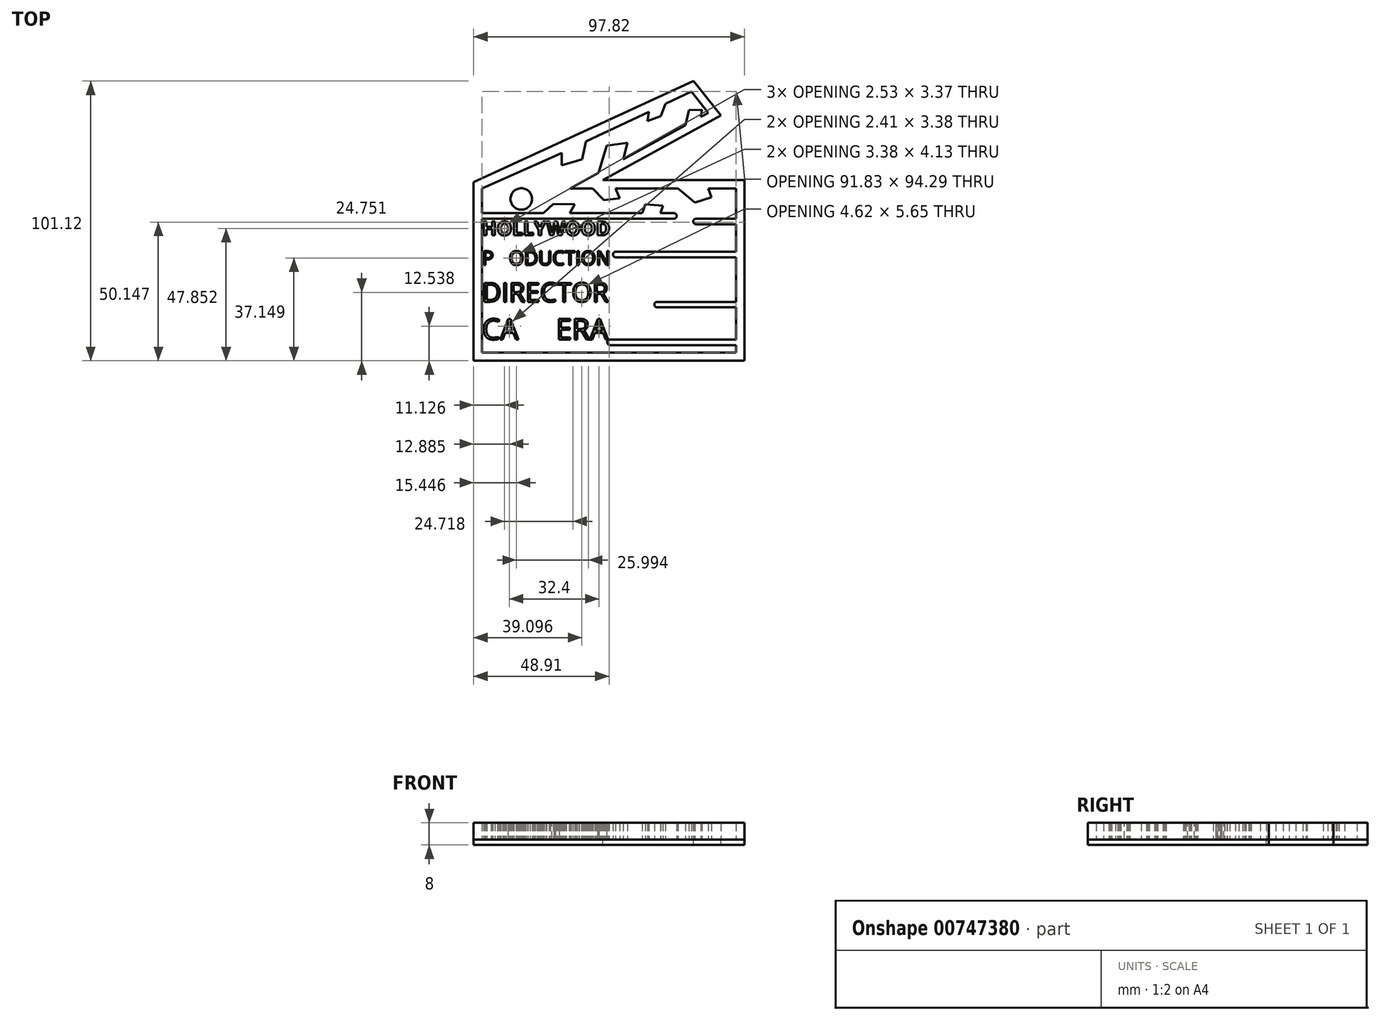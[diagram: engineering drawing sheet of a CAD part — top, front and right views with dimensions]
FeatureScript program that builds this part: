
annotation { "Feature Type Name" : "Feature", "Feature Type Description" : "" }
export const myFeature = defineFeature(function(context is Context, id is Id, definition is map)
    precondition{}
    {
        {
            var Q0;
            Q0=qCreatedBy(makeId("Top.planeOp"),FACE);
            var sketch = newSketch(context, id + "F0", { "sketchPlane" : qUnion([Q0])});
            skLineSegment(sketch, "E0", {"start": v(-11.38, 5.66) * mm, "end": v(-6.26, 5.66) * mm});
            skLineSegment(sketch, "E1", {"start": v(45.56, 5.66) * mm, "end": v(45.56, -5.33) * mm});
            skLineSegment(sketch, "E2", {"start": v(45.56, -53.68) * mm, "end": v(-46.26, -53.68) * mm});
            skLineSegment(sketch, "E3", {"start": v(-46.26, -53.68) * mm, "end": v(-46.26, -16.97) * mm});
            skLineSegment(sketch, "E4", {"start": v(-11.38, 5.66) * mm, "end": v(-14.37, 5.66) * mm});
            skLineSegment(sketch, "E5", {"start": v(-14.37, 5.66) * mm, "end": v(-4.08, 11.29) * mm});
            skLineSegment(sketch, "E6", {"start": v(35.51, 32.95) * mm, "end": v(29.42, 40.61) * mm});
            skLineSegment(sketch, "E7", {"start": v(29.42, 40.61) * mm, "end": v(20.01, 36.15) * mm});
            skLineSegment(sketch, "E8", {"start": v(-17.4, 18.45) * mm, "end": v(-46.26, 5.66) * mm});
            skLineSegment(sketch, "E9", {"start": v(-46.26, 5.66) * mm, "end": v(-46.26, 0) * mm});
            skPoint(sketch, "E10.endSnap0", {"position": v(32.47, 36.78) * mm});
            skPoint(sketch, "E10.end.orphan", {"position": v(30.16, 36.78) * mm});
            skPoint(sketch, "E11.start.orphan", {"position": v(24.87, 32.95) * mm});
            skPoint(sketch, "E12.end.orphan", {"position": v(30.16, 32.95) * mm});
            skLineSegment(sketch, "E13", {"start": v(-46.26, -5.33) * mm, "end": v(23.1, -5.33) * mm});
            skPoint(sketch, "E14.endSnap0", {"position": v(-22.67, 10.91) * mm});
            skLineSegment(sketch, "E15.trimOffspring", {"start": v(31.08, -5.33) * mm, "end": v(45.56, -5.33) * mm});
            skText(sketch, "E16", { "text": "HOLLYWOOD", "fontName": "OpenSans-Bold.ttf"});
            skText(sketch, "E17", { "text": "P   ODUCTION", "fontName": "OpenSans-Regular.ttf"});
            skLineSegment(sketch, "E18", {"start": v(2.08, -17.25) * mm, "end": v(45.56, -17.25) * mm});
            skText(sketch, "E19", { "text": "DIRECTOR", "fontName": "OpenSans-Regular.ttf"});
            skLineSegment(sketch, "E20", {"start": v(0, -35.36) * mm, "end": v(5.2, -35.36) * mm});
            skLineSegment(sketch, "E21.trimOffspring", {"start": v(17.03, -35.36) * mm, "end": v(45.56, -35.36) * mm});
            skPoint(sketch, "E22.end.orphan", {"position": v(17.03, -38.03) * mm});
            skLineSegment(sketch, "E23", {"start": v(-46.26, -28.44) * mm, "end": v(-46.26, -22.04) * mm});
            skText(sketch, "E24", { "text": "CA     ERA", "fontName": "OpenSans-Regular.ttf"});
            skLineSegment(sketch, "E25", {"start": v(0, -48.98) * mm, "end": v(45.56, -48.98) * mm});
            skLineSegment(sketch, "E26.trimOffspring", {"start": v(-46.26, -11.33) * mm, "end": v(-46.26, -5.33) * mm});
            skLineSegment(sketch, "E27", {"start": v(-46.26, -16.97) * mm, "end": v(-46.26, -11.33) * mm});
            skPoint(sketch, "E28.orphan", {"position": v(-18.2, 8) * mm});
            skPoint(sketch, "E29.end.orphan", {"position": v(-27.15, 13.83) * mm});
            skPoint(sketch, "E30.end.orphan", {"position": v(-13.09, 13.83) * mm});
            skPoint(sketch, "E31.end.orphan", {"position": v(-16.1, 2.25) * mm});
            skPoint(sketch, "E14.end.orphan", {"position": v(-22.67, 2.57) * mm});
            skPoint(sketch, "E32.end.orphan", {"position": v(-8.41, -5.33) * mm});
            skPoint(sketch, "E33.end.orphan", {"position": v(-11.38, -2.08) * mm});
            skPoint(sketch, "E34.end.orphan", {"position": v(-0.37, 2.25) * mm});
            skPoint(sketch, "E35.end.orphan", {"position": v(9.85, 5.66) * mm});
            skPoint(sketch, "E36.start.orphan", {"position": v(13.6, 0) * mm});
            skPoint(sketch, "E37.start.orphan", {"position": v(31.92, 0) * mm});
            skPoint(sketch, "E38.end.orphan", {"position": v(45.56, -49.2) * mm});
            skPoint(sketch, "E39.end.orphan", {"position": v(2.16, 24.06) * mm});
            skPoint(sketch, "E39.start.orphan", {"position": v(6.02, 29.53) * mm});
            skPoint(sketch, "E40.end.orphan", {"position": v(-4.66, 24.06) * mm});
            skPoint(sketch, "E41.start.orphan", {"position": v(24.87, 30.37) * mm});
            skLineSegment(sketch, "E42", {"start": v(32.89, 31.51) * mm, "end": v(33.25, 34.06) * mm});
            skLineSegment(sketch, "E43", {"start": v(28.6, 33.96) * mm, "end": v(27.23, 28.42) * mm});
            skPoint(sketch, "E44.start.orphan", {"position": v(19.09, 32.53) * mm});
            skPoint(sketch, "E45.end.orphan", {"position": v(12.32, 32.53) * mm});
            skLineSegment(sketch, "E46", {"start": v(20.01, 36.15) * mm, "end": v(18.36, 31.75) * mm});
            skLineSegment(sketch, "E47", {"start": v(18.36, 31.75) * mm, "end": v(13.56, 30) * mm});
            skLineSegment(sketch, "E48", {"start": v(13.56, 30) * mm, "end": v(14.08, 33.34) * mm});
            skLineSegment(sketch, "E49", {"start": v(6.26, 22.13) * mm, "end": v(4.75, 16.12) * mm});
            skLineSegment(sketch, "E50", {"start": v(6.26, 22.13) * mm, "end": v(-1.14, 21.04) * mm});
            skLineSegment(sketch, "E51", {"start": v(-1.14, 21.04) * mm, "end": v(-4.08, 11.29) * mm});
            skLineSegment(sketch, "E52", {"start": v(-10.08, 16.13) * mm, "end": v(-8.63, 22.6) * mm});
            skLineSegment(sketch, "E53", {"start": v(-10.08, 16.13) * mm, "end": v(-17.39, 13.94) * mm});
            skLineSegment(sketch, "E54", {"start": v(-17.39, 13.94) * mm, "end": v(-17.39, 18.45) * mm});
            skLineSegment(sketch, "E55", {"start": v(-24.05, -3.33) * mm, "end": v(-20.53, 0) * mm});
            skLineSegment(sketch, "E56", {"start": v(-12.76, -0.05) * mm, "end": v(-14.53, -3.33) * mm});
            skLineSegment(sketch, "E57", {"start": v(-6.26, 5.66) * mm, "end": v(-2.16, 1.44) * mm});
            skLineSegment(sketch, "E58", {"start": v(-2.16, 1.44) * mm, "end": v(3.48, 2) * mm});
            skLineSegment(sketch, "E59", {"start": v(3.48, 2) * mm, "end": v(1.98, 5.66) * mm});
            skPoint(sketch, "E60.end.orphan", {"position": v(10.94, -5.33) * mm});
            skPoint(sketch, "E61.end.orphan", {"position": v(18.64, -5.33) * mm});
            skLineSegment(sketch, "E62", {"start": v(12.77, -0.05) * mm, "end": v(11.64, -3.33) * mm});
            skLineSegment(sketch, "E63", {"start": v(12.77, -0.05) * mm, "end": v(19.1, -0.66) * mm});
            skLineSegment(sketch, "E64", {"start": v(19.1, -0.66) * mm, "end": v(18.3, -3.33) * mm});
            skLineSegment(sketch, "E65", {"start": v(24.63, 5.66) * mm, "end": v(30.73, 0.5) * mm});
            skLineSegment(sketch, "E66", {"start": v(30.73, 0.5) * mm, "end": v(36.62, 2.38) * mm});
            skLineSegment(sketch, "E67", {"start": v(36.62, 2.38) * mm, "end": v(35.55, 5.66) * mm});
            skLineSegment(sketch, "E68.0", {"start": v(-49.26, -16.98) * mm, "end": v(-49.26, -11.33) * mm});
            skLineSegment(sketch, "E68.1", {"start": v(-49.26, -11.33) * mm, "end": v(-49.26, 0) * mm});
            skLineSegment(sketch, "E68.2", {"start": v(-49.26, 5.58) * mm, "end": v(-49.26, 0) * mm});
            skLineSegment(sketch, "E69.0", {"start": v(-49.26, -54.37) * mm, "end": v(-49.26, -16.98) * mm});
            skLineSegment(sketch, "E70.0", {"start": v(-2.64, 8.66) * mm, "end": v(40.08, 32.03) * mm});
            skLineSegment(sketch, "E71.0", {"start": v(-2.64, 8.66) * mm, "end": v(48.56, 8.66) * mm});
            skLineSegment(sketch, "E72.0", {"start": v(48.56, 8.6) * mm, "end": v(48.56, -56.68) * mm});
            skLineSegment(sketch, "E73", {"start": v(48.56, 8.6) * mm, "end": v(48.56, 8.66) * mm});
            skLineSegment(sketch, "E74", {"start": v(48.56, 8.66) * mm, "end": v(48.56, 8.66) * mm});
            skLineSegment(sketch, "E75.0", {"start": v(45.13, -56.68) * mm, "end": v(-46.22, -56.68) * mm});
            skLineSegment(sketch, "E76", {"start": v(-46.22, -56.68) * mm, "end": v(-49.26, -56.68) * mm});
            skLineSegment(sketch, "E77", {"start": v(-49.26, -56.68) * mm, "end": v(-49.26, -54.37) * mm});
            skLineSegment(sketch, "E78", {"start": v(45.13, -56.68) * mm, "end": v(48.56, -56.68) * mm});
            skLineSegment(sketch, "E79", {"start": v(48.56, -56.68) * mm, "end": v(48.56, -56.68) * mm});
            skLineSegment(sketch, "E80", {"start": v(28.6, 33.96) * mm, "end": v(33.25, 34.06) * mm});
            skLineSegment(sketch, "E81.trimOffspring", {"start": v(32.89, 31.51) * mm, "end": v(35.51, 32.95) * mm});
            skPoint(sketch, "E82.end.orphan", {"position": v(39.94, 32.95) * mm});
            skLineSegment(sketch, "E83", {"start": v(40.08, 32.03) * mm, "end": v(40.08, 32.03) * mm});
            skLineSegment(sketch, "E84.0", {"start": v(2.08, -19.25) * mm, "end": v(45.56, -19.25) * mm});
            skLineSegment(sketch, "E85.0", {"start": v(17.03, -37.36) * mm, "end": v(45.56, -37.36) * mm});
            skLineSegment(sketch, "E86.0", {"start": v(31.08, -7.33) * mm, "end": v(45.56, -7.33) * mm});
            skLineSegment(sketch, "E87.0", {"start": v(-46.22, -3.33) * mm, "end": v(-24.05, -3.33) * mm});
            skLineSegment(sketch, "E88.0", {"start": v(0, -50.98) * mm, "end": v(45.56, -50.98) * mm});
            skLineSegment(sketch, "E89.trimOffspring", {"start": v(14.08, 33.34) * mm, "end": v(-8.63, 22.6) * mm});
            skLineSegment(sketch, "E90.trimOffspring", {"start": v(4.75, 16.12) * mm, "end": v(27.23, 28.42) * mm});
            skLineSegment(sketch, "E91.trimOffspring", {"start": v(-17.39, 18.45) * mm, "end": v(-17.4, 18.45) * mm});
            skLineSegment(sketch, "E92.trimOffspring", {"start": v(1.98, 5.66) * mm, "end": v(24.63, 5.66) * mm});
            skLineSegment(sketch, "E93.trimOffspring", {"start": v(35.55, 5.66) * mm, "end": v(45.56, 5.66) * mm});
            skLineSegment(sketch, "E94.trimOffspring", {"start": v(-14.53, -3.33) * mm, "end": v(11.64, -3.33) * mm});
            skLineSegment(sketch, "E95.trimOffspring", {"start": v(18.3, -3.33) * mm, "end": v(23.1, -3.33) * mm});
            skArc(sketch, "E96", {"start": v(23.1, -3.33) * mm, "mid": v(24.1, -4.33) * mm, "end": v(23.1, -5.33) * mm});
            skArc(sketch, "E97", {"start": v(31.08, -5.33) * mm, "mid": v(30.08, -6.33) * mm, "end": v(31.08, -7.33) * mm});
            skArc(sketch, "E98", {"start": v(2.08, -17.25) * mm, "mid": v(1.08, -18.25) * mm, "end": v(2.08, -19.25) * mm});
            skLineSegment(sketch, "E99.0", {"start": v(0, -37.36) * mm, "end": v(5.2, -37.36) * mm});
            skArc(sketch, "E100", {"start": v(17.03, -37.36) * mm, "mid": v(16.03, -36.36) * mm, "end": v(17.03, -35.36) * mm});
            skArc(sketch, "E101", {"start": v(5.2, -35.36) * mm, "mid": v(6.2, -36.36) * mm, "end": v(5.2, -37.36) * mm});
            skPoint(sketch, "E102.center.orphan", {"position": v(-36.76, 0) * mm});
            skPoint(sketch, "E103.endSnap0", {"position": v(-31.83, 12.05) * mm});
            skCircle(sketch, "E104", {"center": v(-32.06, 1.81) * mm, "radius": 3.9 * mm});
            skPoint(sketch, "E103.end.orphan", {"position": v(-31.83, 6) * mm});
            skPoint(sketch, "E105.start.orphan", {"position": v(28.13, 43.32) * mm});
            skLineSegment(sketch, "E106", {"start": v(30.21, 44.44) * mm, "end": v(-49.26, 7.84) * mm});
            skLineSegment(sketch, "E107", {"start": v(-49.26, 5.58) * mm, "end": v(-49.26, 7.84) * mm});
            skLineSegment(sketch, "E108", {"start": v(30.21, 44.44) * mm, "end": v(40.08, 32.03) * mm});
            skArc(sketch, "E109", {"start": v(0, -35.36) * mm, "mid": v(-1, -36.36) * mm, "end": v(0, -37.36) * mm});
            skArc(sketch, "E110", {"start": v(0, -48.98) * mm, "mid": v(-1, -49.98) * mm, "end": v(0, -50.98) * mm});
            skLineSegment(sketch, "E111.trimOffspring", {"start": v(45.56, -7.33) * mm, "end": v(45.56, -17.25) * mm});
            skLineSegment(sketch, "E112.trimOffspring", {"start": v(45.56, -19.25) * mm, "end": v(45.56, -35.36) * mm});
            skLineSegment(sketch, "E113.trimOffspring", {"start": v(45.56, -50.98) * mm, "end": v(45.56, -53.68) * mm});
            skLineSegment(sketch, "E114", {"start": v(-46.22, -3.33) * mm, "end": v(-46.26, 0) * mm});
            skPoint(sketch, "E115.start.orphan", {"position": v(12.56, 0) * mm});
            skLineSegment(sketch, "E116.trimOffspring", {"start": v(45.56, -37.36) * mm, "end": v(45.56, -48.98) * mm});
            skLineSegment(sketch, "E117", {"start": v(-20.53, 0) * mm, "end": v(-12.76, -0.05) * mm});
            const initialGuessF0  = {"E16": [-0.04626, -0.01133, 1, 0, 0.00503], "E17": [-0.04626, -0.02204, 1, 0, 0.00506], "E19": [-0.04626, -0.03536, 1, 0, 0.00692], "E24": [-0.04626, -0.04898, 1, 0, 0.00751]};
            skSetInitialGuess(sketch, initialGuessF0);
            skSolve(sketch);
        }
        {
            var Q0;
            Q0=makeQuery(id+"F0.imprint","IMPRINT",FACE,{"disambiguationData":[TD([[makeQuery(id+"F0.imprint","IMPRINT",EDGE,{"derivedFrom":sQuery(id+"F0.wireOp",EDGE,"E16.sketch_text.stroke-47")}),-1.0]])]});
            var Q1;
            Q1=makeQuery(id+"F0.imprint","IMPRINT",FACE,{"disambiguationData":[TD([[makeQuery(id+"F0.imprint","IMPRINT",EDGE,{"derivedFrom":sQuery(id+"F0.wireOp",EDGE,"E16.sketch_text.stroke-38")}),-1.0]])]});
            var Q2;
            Q2=makeQuery(id+"F0.imprint","IMPRINT",FACE,{"disambiguationData":[TD([[makeQuery(id+"F0.imprint","IMPRINT",EDGE,{"derivedFrom":sQuery(id+"F0.wireOp",EDGE,"E16.sketch_text.stroke-32")}),-1.0]])]});
            var Q3;
            Q3=makeQuery(id+"F0.imprint","IMPRINT",FACE,{"disambiguationData":[TD([[makeQuery(id+"F0.imprint","IMPRINT",EDGE,{"derivedFrom":sQuery(id+"F0.wireOp",EDGE,"E16.sketch_text.stroke-26")}),-1.0]])]});
            var Q4;
            Q4=makeQuery(id+"F0.imprint","IMPRINT",FACE,{"disambiguationData":[TD([[makeQuery(id+"F0.imprint","IMPRINT",EDGE,{"derivedFrom":sQuery(id+"F0.wireOp",EDGE,"E16.sketch_text.stroke-12")}),-1.0]])]});
            var Q5;
            Q5=makeQuery(id+"F0.imprint","IMPRINT",FACE,{"disambiguationData":[TD([[makeQuery(id+"F0.imprint","IMPRINT",EDGE,{"derivedFrom":sQuery(id+"F0.wireOp",EDGE,"E16.sketch_text.stroke-0")}),-1.0]])]});
            var Q6;
            Q6=makeQuery(id+"F0.imprint","IMPRINT",FACE,{"disambiguationData":[TD([[makeQuery(id+"F0.imprint","IMPRINT",EDGE,{"derivedFrom":sQuery(id+"F0.wireOp",EDGE,"E16.sketch_text.stroke-99")}),-1.0]])]});
            var Q7;
            Q7=makeQuery(id+"F0.imprint","IMPRINT",FACE,{"disambiguationData":[TD([[makeQuery(id+"F0.imprint","IMPRINT",EDGE,{"derivedFrom":sQuery(id+"F0.wireOp",EDGE,"E16.sketch_text.stroke-85")}),-1.0]])]});
            var Q8;
            Q8=makeQuery(id+"F0.imprint","IMPRINT",FACE,{"disambiguationData":[TD([[makeQuery(id+"F0.imprint","IMPRINT",EDGE,{"derivedFrom":sQuery(id+"F0.wireOp",EDGE,"E16.sketch_text.stroke-71")}),-1.0]])]});
            var Q9;
            Q9=makeQuery(id+"F0.imprint","IMPRINT",FACE,{"disambiguationData":[TD([[makeQuery(id+"F0.imprint","IMPRINT",EDGE,{"derivedFrom":sQuery(id+"F0.wireOp",EDGE,"E17.sketch_text.stroke-0")}),-1.0]])]});
            var Q10;
            Q10=makeQuery(id+"F0.imprint","IMPRINT",FACE,{"disambiguationData":[TD([[makeQuery(id+"F0.imprint","IMPRINT",EDGE,{"derivedFrom":sQuery(id+"F0.wireOp",EDGE,"E17.sketch_text.stroke-15")}),-1.0]])]});
            var Q11;
            Q11=makeQuery(id+"F0.imprint","IMPRINT",FACE,{"disambiguationData":[TD([[makeQuery(id+"F0.imprint","IMPRINT",EDGE,{"derivedFrom":sQuery(id+"F0.wireOp",EDGE,"E17.sketch_text.stroke-31")}),-1.0]])]});
            var Q12;
            Q12=makeQuery(id+"F0.imprint","IMPRINT",FACE,{"disambiguationData":[TD([[makeQuery(id+"F0.imprint","IMPRINT",EDGE,{"derivedFrom":sQuery(id+"F0.wireOp",EDGE,"E17.sketch_text.stroke-45")}),-1.0]])]});
            var Q13;
            Q13=makeQuery(id+"F0.imprint","IMPRINT",FACE,{"disambiguationData":[TD([[makeQuery(id+"F0.imprint","IMPRINT",EDGE,{"derivedFrom":sQuery(id+"F0.wireOp",EDGE,"E17.sketch_text.stroke-59")}),-1.0]])]});
            var Q14;
            Q14=makeQuery(id+"F0.imprint","IMPRINT",FACE,{"disambiguationData":[TD([[makeQuery(id+"F0.imprint","IMPRINT",EDGE,{"derivedFrom":sQuery(id+"F0.wireOp",EDGE,"E17.sketch_text.stroke-74")}),-1.0]])]});
            var Q15;
            Q15=makeQuery(id+"F0.imprint","IMPRINT",FACE,{"disambiguationData":[TD([[makeQuery(id+"F0.imprint","IMPRINT",EDGE,{"derivedFrom":sQuery(id+"F0.wireOp",EDGE,"E17.sketch_text.stroke-82")}),-1.0]])]});
            var Q16;
            Q16=makeQuery(id+"F0.imprint","IMPRINT",FACE,{"disambiguationData":[TD([[makeQuery(id+"F0.imprint","IMPRINT",EDGE,{"derivedFrom":sQuery(id+"F0.wireOp",EDGE,"E17.sketch_text.stroke-86")}),-1.0]])]});
            var Q17;
            Q17=makeQuery(id+"F0.imprint","IMPRINT",FACE,{"disambiguationData":[TD([[makeQuery(id+"F0.imprint","IMPRINT",EDGE,{"derivedFrom":sQuery(id+"F0.wireOp",EDGE,"E17.sketch_text.stroke-102")}),-1.0]])]});
            var Q18;
            Q18=makeQuery(id+"F0.imprint","IMPRINT",FACE,{"disambiguationData":[TD([[makeQuery(id+"F0.imprint","IMPRINT",EDGE,{"derivedFrom":sQuery(id+"F0.wireOp",EDGE,"E19.sketch_text.stroke-0")}),-1.0]])]});
            var Q19;
            Q19=makeQuery(id+"F0.imprint","IMPRINT",FACE,{"disambiguationData":[TD([[makeQuery(id+"F0.imprint","IMPRINT",EDGE,{"derivedFrom":sQuery(id+"F0.wireOp",EDGE,"E19.sketch_text.stroke-14")}),-1.0]])]});
            var Q20;
            Q20=makeQuery(id+"F0.imprint","IMPRINT",FACE,{"disambiguationData":[TD([[makeQuery(id+"F0.imprint","IMPRINT",EDGE,{"derivedFrom":sQuery(id+"F0.wireOp",EDGE,"E19.sketch_text.stroke-18")}),-1.0]])]});
            var Q21;
            Q21=makeQuery(id+"F0.imprint","IMPRINT",FACE,{"disambiguationData":[TD([[makeQuery(id+"F0.imprint","IMPRINT",EDGE,{"derivedFrom":sQuery(id+"F0.wireOp",EDGE,"E19.sketch_text.stroke-36")}),-1.0]])]});
            var Q22;
            Q22=makeQuery(id+"F0.imprint","IMPRINT",FACE,{"disambiguationData":[TD([[makeQuery(id+"F0.imprint","IMPRINT",EDGE,{"derivedFrom":sQuery(id+"F0.wireOp",EDGE,"E19.sketch_text.stroke-48")}),-1.0]])]});
            var Q23;
            Q23=makeQuery(id+"F0.imprint","IMPRINT",FACE,{"disambiguationData":[TD([[makeQuery(id+"F0.imprint","IMPRINT",EDGE,{"derivedFrom":sQuery(id+"F0.wireOp",EDGE,"E19.sketch_text.stroke-63")}),-1.0]])]});
            var Q24;
            Q24=makeQuery(id+"F0.imprint","IMPRINT",FACE,{"disambiguationData":[TD([[makeQuery(id+"F0.imprint","IMPRINT",EDGE,{"derivedFrom":sQuery(id+"F0.wireOp",EDGE,"E19.sketch_text.stroke-71")}),-1.0]])]});
            var Q25;
            Q25=makeQuery(id+"F0.imprint","IMPRINT",FACE,{"disambiguationData":[TD([[makeQuery(id+"F0.imprint","IMPRINT",EDGE,{"derivedFrom":sQuery(id+"F0.wireOp",EDGE,"E19.sketch_text.stroke-87")}),-1.0]])]});
            var Q26;
            Q26=makeQuery(id+"F0.imprint","IMPRINT",FACE,{"disambiguationData":[TD([[makeQuery(id+"F0.imprint","IMPRINT",EDGE,{"derivedFrom":sQuery(id+"F0.wireOp",EDGE,"E24.sketch_text.stroke-0")}),-1.0]])]});
            var Q27;
            Q27=makeQuery(id+"F0.imprint","IMPRINT",FACE,{"disambiguationData":[TD([[makeQuery(id+"F0.imprint","IMPRINT",EDGE,{"derivedFrom":sQuery(id+"F0.wireOp",EDGE,"E24.sketch_text.stroke-15")}),-1.0]])]});
            var Q28;
            Q28=makeQuery(id+"F0.imprint","IMPRINT",FACE,{"disambiguationData":[TD([[makeQuery(id+"F0.imprint","IMPRINT",EDGE,{"derivedFrom":sQuery(id+"F0.wireOp",EDGE,"E24.sketch_text.stroke-28")}),-1.0]])]});
            var Q29;
            Q29=makeQuery(id+"F0.imprint","IMPRINT",FACE,{"disambiguationData":[TD([[makeQuery(id+"F0.imprint","IMPRINT",EDGE,{"derivedFrom":sQuery(id+"F0.wireOp",EDGE,"E24.sketch_text.stroke-40")}),-1.0]])]});
            var Q30;
            Q30=makeQuery(id+"F0.imprint","IMPRINT",FACE,{"disambiguationData":[TD([[makeQuery(id+"F0.imprint","IMPRINT",EDGE,{"derivedFrom":sQuery(id+"F0.wireOp",EDGE,"E24.sketch_text.stroke-58")}),-1.0]])]});
            var Q31;
            Q31=makeQuery(id+"F0.imprint","IMPRINT",FACE,{"disambiguationData":[TD([[makeQuery(id+"F0.imprint","IMPRINT",EDGE,{"derivedFrom":sQuery(id+"F0.wireOp",EDGE,"E0")}),1.0]])]});
            var Q32;
            Q32=makeQuery(id+"F0.imprint","IMPRINT",FACE,{"disambiguationData":[TD([[makeQuery(id+"F0.imprint","IMPRINT",EDGE,{"derivedFrom":sQuery(id+"F0.wireOp",EDGE,"E104")}),1.0]])]});
            extrude(context, id + "F1", {"entities" : qUnion([Q0, Q1, Q2, Q3, Q4, Q5, Q6, Q7, Q8, Q9, Q10, Q11, Q12, Q13, Q14, Q15, Q16, Q17, Q18, Q19, Q20, Q21, Q22, Q23, Q24, Q25, Q26, Q27, Q28, Q29, Q30, Q31, Q32]), "depth" : 6 * mm, "offsetDistance" : 25 * mm});
        }
        {
            var Q0;
            Q0=qCreatedBy(makeId("Top.planeOp"),FACE);
            var sketch = newSketch(context, id + "F2", { "sketchPlane" : qUnion([Q0])});
            skLineSegment(sketch, "E118.0", {"start": v(-2.64, 8.66) * mm, "end": v(40.08, 32.03) * mm});
            skLineSegment(sketch, "E119.0", {"start": v(-2.64, 8.66) * mm, "end": v(48.56, 8.66) * mm});
            skLineSegment(sketch, "E120.0", {"start": v(48.56, 8.66) * mm, "end": v(48.56, -56.68) * mm});
            skLineSegment(sketch, "E121.0", {"start": v(48.56, -56.68) * mm, "end": v(-49.26, -56.68) * mm});
            skLineSegment(sketch, "E122.0", {"start": v(-49.26, -56.68) * mm, "end": v(-49.26, 7.84) * mm});
            skLineSegment(sketch, "E123.0", {"start": v(30.21, 44.44) * mm, "end": v(-49.26, 7.84) * mm});
            skPoint(sketch, "E124.0", {"position": v(35.15, 38.24) * mm});
            skLineSegment(sketch, "E125.0", {"start": v(30.21, 44.44) * mm, "end": v(40.08, 32.03) * mm});
            skSolve(sketch);
        }
        {
            var Q0;
            Q0 = qSketchRegion(id + "F2", true);
            extrude(context, id + "F3", {"entities" : qUnion([Q0]), "oppositeDirection" : true, "depth" : 2 * mm, "offsetDistance" : 25 * mm});
        }
    });
